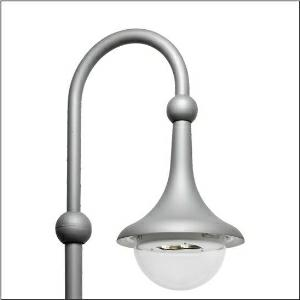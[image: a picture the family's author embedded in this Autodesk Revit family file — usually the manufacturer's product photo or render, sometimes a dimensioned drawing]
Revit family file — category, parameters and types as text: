
# Revit family: grosse_glocke_iq___st1_2a_5xa1565a1f108_90a8
name_source: partatom
category: Lighting Fixtures
units: mm (PartAtom-declared; Revit-internal decimal feet)

## family parameters
Cut with Voids When Loaded = No
Host = Face
Light Source = No
Part Type = Normal
Room Calculation Point = No
Round Connector Dimension = Use Diameter
Shared = No

## types (1)
- --- (1 x LED, 4180 lm, 34.3 W, 2200K)
    Apparent Load = 34 VA
    CIE Flux Codes = 28 66 95 100 100
    Color Rendering = 70
    Color Temperature = 2200K
    Default Elevation = 1800 mm
    Description = Large Bell iQ, mast luminaire, primary light control with 3 zone facetted reflector, of plastic, silver coated, primary optical cover: enclosure, of PMMA, transparent, light distribution: ST1.2a, light emission: direct distribution, primary light characteristic: asymmetric, installation type: suspended mounting, High Power LED, rated luminous flux: 4.180lm, luminous efficacy: 122lm/W, light colour: 722, colour temperature: 2200K, control gear: iQ Street-Remote, control: optimised constant luminous flux control (CLO 2.0), Desk-Remote (wireless, voltage-free reading and setting of iQ features in the workshop via application-optimized NFC function/RFID function), Light-Fading, Smart-Wire, Night-Set, Lumen-Switch, Temp-Guard, Auto-Match, Street-Remote, pre-setting: logarithmic dimming characteristic, mains connection: 230..240V, AC, 50/60Hz, start of lifetime: 34W, end of service life: 38W, reduction: 16W, luminaire housing, bell-shaped, of glass-fibre reinforced polyester, coated, Siteco® metallic grey (DB 702S), please order curved mast extension separately, diameter: 530mm, height: 695mm, mounting height: 4..6m, protection rating (complete): IP54, insulation class (complete): insulation class II (safety insulation), certification: CE, ENEC, VDE, impact resistance: IK08, standard-compliant lighting for roads and squares, packaging unit: 1 piece

Light Distribution: ST1.2a
    Height = 695 mm
    Lamp = 1 x LED
    Lamp Light Flux = 4180 lm
    Lamp Power = 34.3 W
    Lamp count = 1
    Length = 530 mm
    Luminous efficacy = 122 lm/W
    Manufacturer = Siteco
    ModVariant = No
    Model = 5XA1565A1F108
    Number of Poles = 1
    OnlyDefault = Yes
    Power Factor = 1
    Product Name = Große Glocke iQ | ST1.2a
    Product group = mast luminaire | pylon annexe
    ProductGroupID = 6200
    Protection Class = Protection class II
    Protection Degree = IP 54
    RLX_Detail_Level = 1
    RLX_Emergency_Light_Flux = 0 lm
    RLX_Emergency_Type = 0
    RLX_Emergency_Type_DB = No
    RlxData = <blob elided: 85389 chars, md5=a10abe4e>
    Socket = socket
    Standby Power = 0 W
    System Light Flux = 4180 lm
    System Power = 34 W
    Type Comments = factory setting: luminous flux: 100 % | dim-lin: 254 | 640 mA
    Type Image = l_1347688.jpg
    URL = http://relux.com
    VarID = @adj_066313
    Voltage = 0 V
    Weight = 0.00 kg
    Width = 0 mm  [stored 0 ft]

note: [stored X ft] marks values corroborated as IEEE doubles in the binary element streams (Revit-internal decimal feet)

## geometry (parser evidence)
native form markers: Blend x4, Sweep x12
no freeform markers — native parametric forms only
